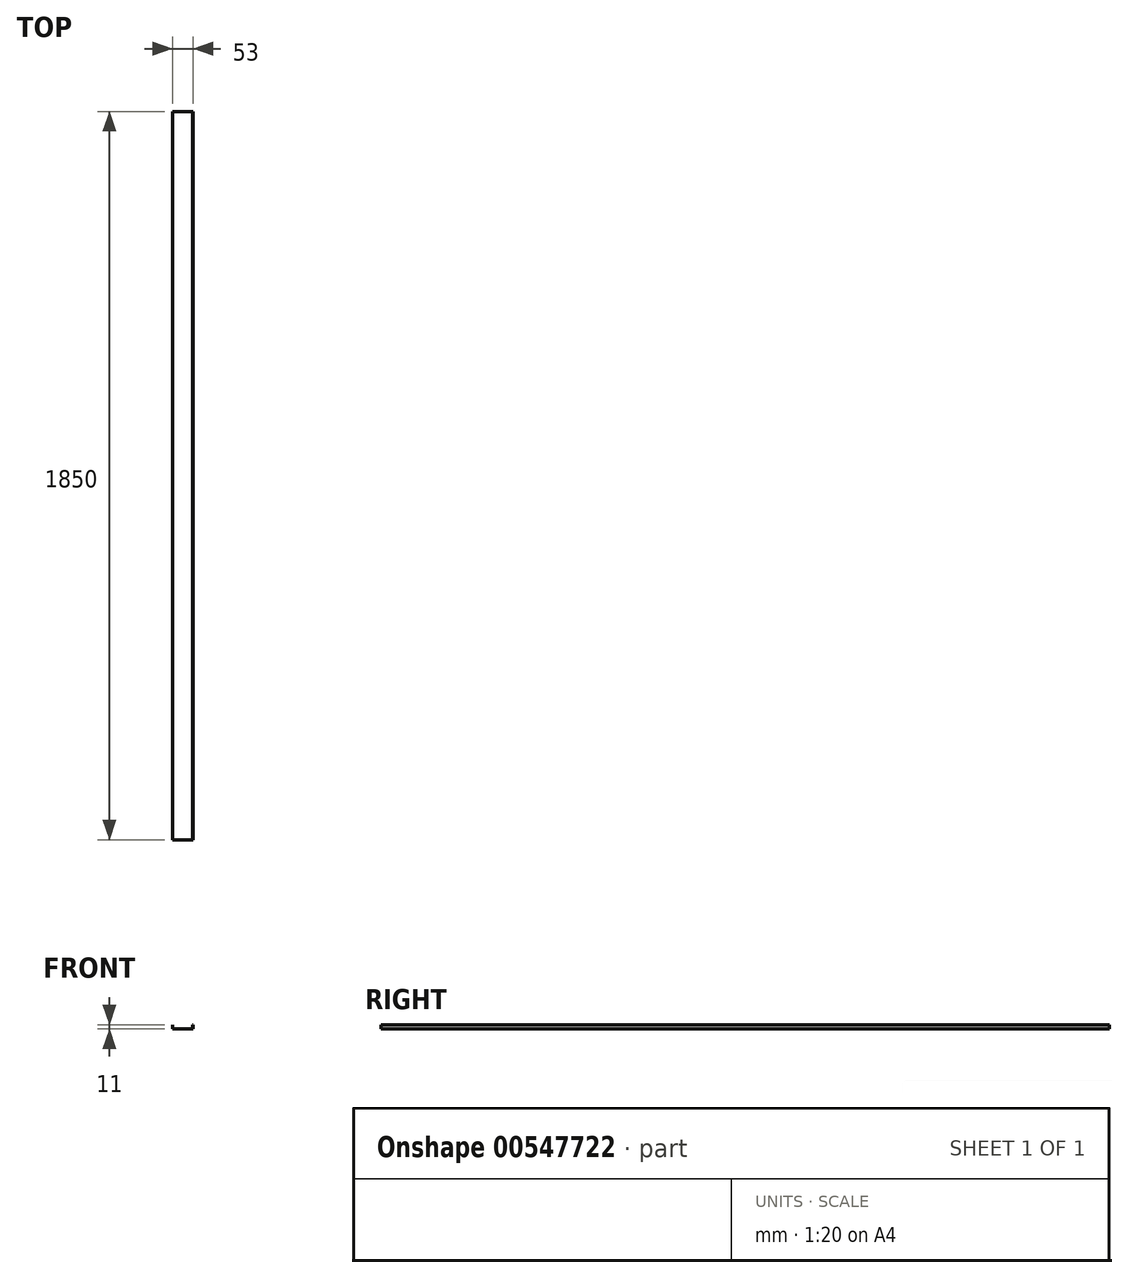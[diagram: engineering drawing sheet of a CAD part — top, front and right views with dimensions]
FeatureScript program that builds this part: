
annotation { "Feature Type Name" : "Feature", "Feature Type Description" : "" }
export const myFeature = defineFeature(function(context is Context, id is Id, definition is map)
    precondition{}
    {
        {
            var Q0;
            Q0=qCreatedBy(makeId("Front.planeOp"),FACE);
            var sketch = newSketch(context, id + "F0", { "sketchPlane" : qUnion([Q0])});
            skLineSegment(sketch, "E0", {"start": v(-26.5, 0) * mm, "end": v(26.5, 0) * mm});
            skLineSegment(sketch, "E1", {"start": v(26.5, 0) * mm, "end": v(26.5, 11) * mm});
            skLineSegment(sketch, "E2", {"start": v(26.5, 11) * mm, "end": v(25.5, 11) * mm});
            skLineSegment(sketch, "E3", {"start": v(25.5, 11) * mm, "end": v(25.5, 1) * mm});
            skLineSegment(sketch, "E4", {"start": v(25.5, 1) * mm, "end": v(-25.5, 1) * mm});
            skLineSegment(sketch, "E5", {"start": v(-25.5, 1) * mm, "end": v(-25.5, 11) * mm});
            skLineSegment(sketch, "E6", {"start": v(-25.5, 11) * mm, "end": v(-26.5, 11) * mm});
            skLineSegment(sketch, "E7", {"start": v(-26.5, 11) * mm, "end": v(-26.5, 0) * mm});
            skSolve(sketch);
        }
        {
            var Q0;
            Q0 = qSketchRegion(id + "F0", true);
            extrude(context, id + "F1", {"entities" : qUnion([Q0]), "depth" : 1850 * mm, "offsetDistance" : 25 * mm});
        }
    });
